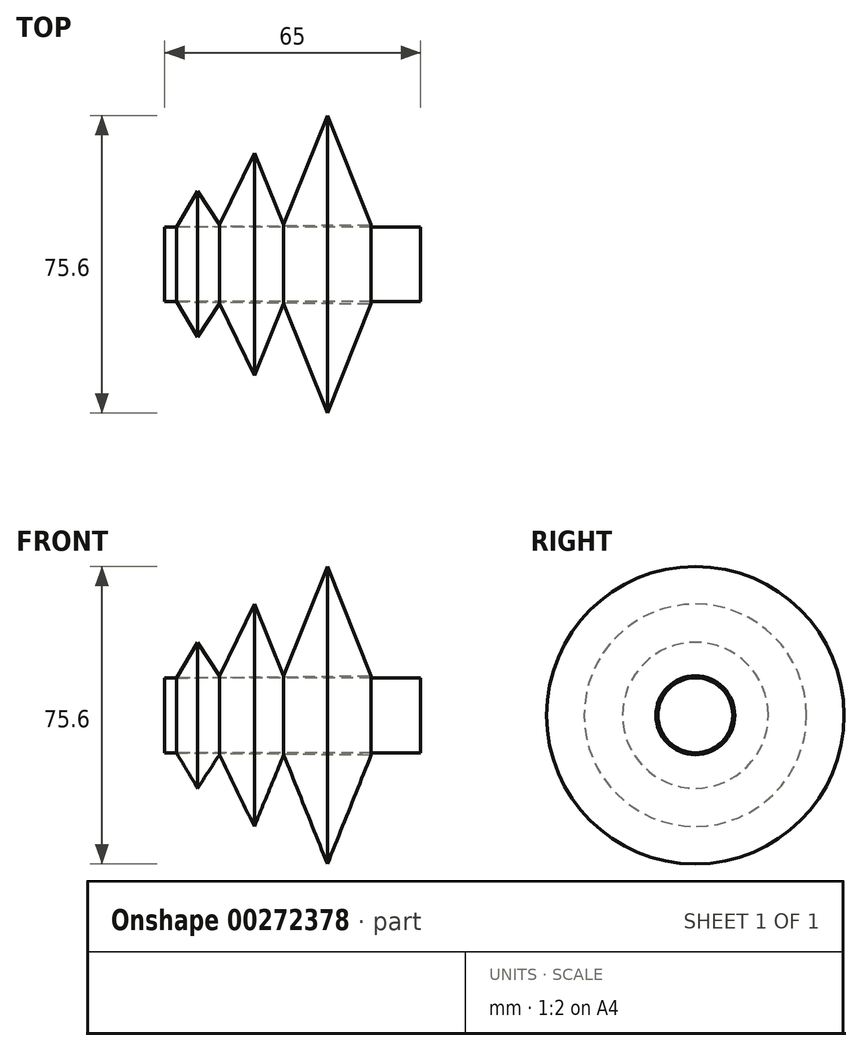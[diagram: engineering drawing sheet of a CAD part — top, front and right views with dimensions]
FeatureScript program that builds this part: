
annotation { "Feature Type Name" : "Feature", "Feature Type Description" : "" }
export const myFeature = defineFeature(function(context is Context, id is Id, definition is map)
    precondition{}
    {
        {
            var Q0;
            Q0=qCreatedBy(makeId("Right.planeOp"),FACE);
            var sketch = newSketch(context, id + "F0", { "sketchPlane" : qUnion([Q0])});
            skCircle(sketch, "E0", {"center": v(0, 0) * mm, "radius": 9.5 * mm});
            skSolve(sketch);
        }
        {
            var Q0;
            Q0 = qSketchRegion(id + "F0", true);
            extrude(context, id + "F1", {"entities" : qUnion([Q0]), "depth" : 65 * mm});
        }
        {
            var Q0;
            Q0=qCreatedBy(makeId("Front.planeOp"),FACE);
            var sketch = newSketch(context, id + "F2", { "sketchPlane" : qUnion([Q0])});
            skLineSegment(sketch, "E1", {"start": v(2.96, 9.5) * mm, "end": v(8.34, 18.53) * mm});
            skLineSegment(sketch, "E2", {"start": v(8.34, 18.53) * mm, "end": v(13.9, 10.02) * mm});
            skLineSegment(sketch, "E3", {"start": v(13.9, 10.02) * mm, "end": v(22.75, 28.25) * mm});
            skLineSegment(sketch, "E4", {"start": v(22.75, 28.25) * mm, "end": v(30.21, 10.02) * mm});
            skLineSegment(sketch, "E5", {"start": v(30.21, 10.02) * mm, "end": v(41.32, 37.8) * mm});
            skLineSegment(sketch, "E6", {"start": v(41.32, 37.8) * mm, "end": v(52.43, 10.02) * mm});
            skLineSegment(sketch, "E7", {"start": v(52.43, 10.02) * mm, "end": v(2.96, 9.5) * mm});
            skSolve(sketch);
        }
        {
            var Q0;
            Q0 = qSketchRegion(id + "F2", true);
            var Q1;
            Q1=makeQuery(id+"F1.opExtrude","SWEPT_FACE",FACE,{"disambiguationData":[OSD([sQuery(id+"F0.wireOp",EDGE,"E0")])]});
            revolve(context, id + "F3", {"entities" : qUnion([Q0]), "axis" : qUnion([Q1]), "revolveType" : RevolveType.FULL});
        }
    });
